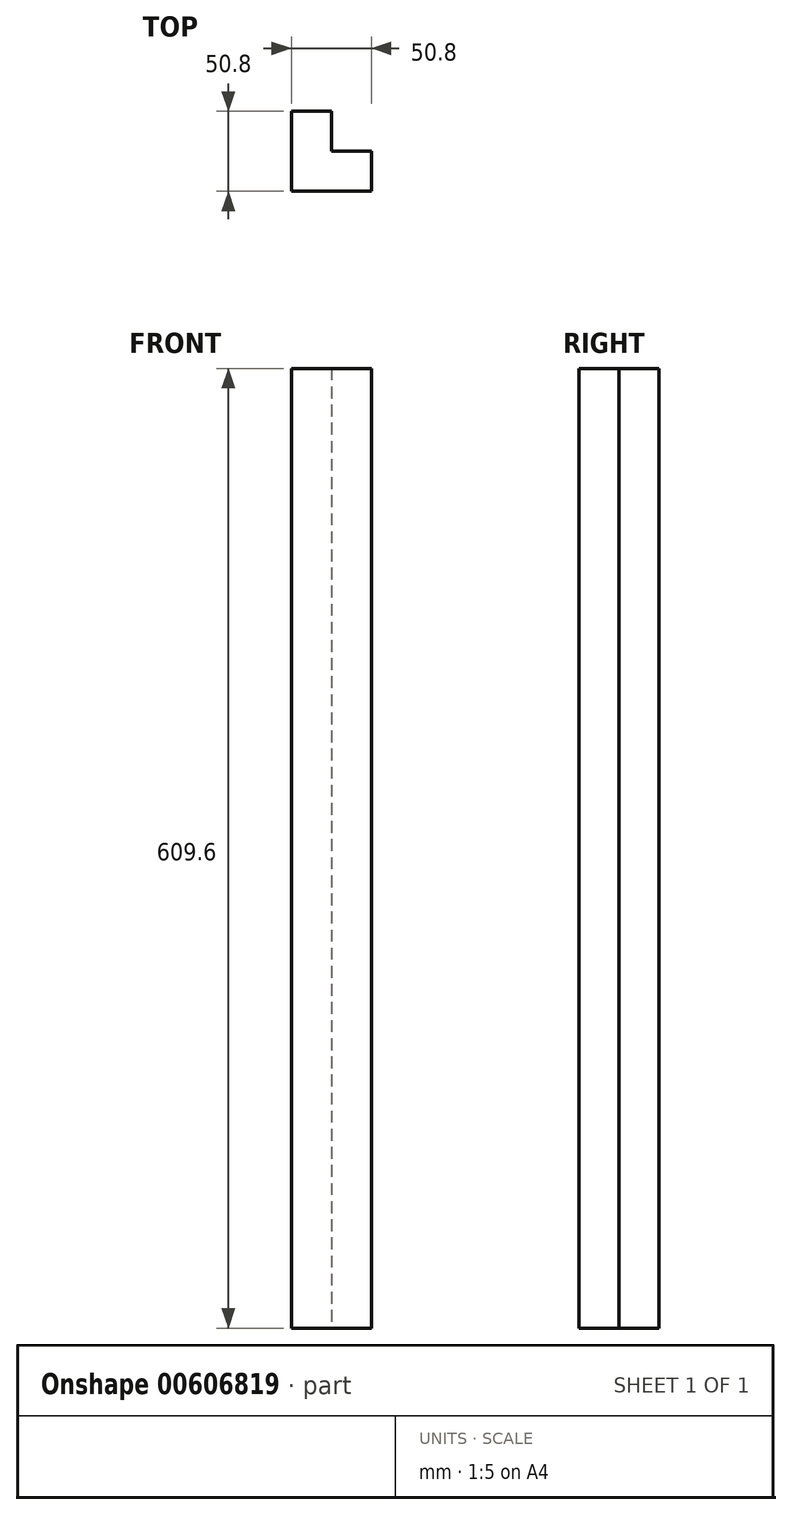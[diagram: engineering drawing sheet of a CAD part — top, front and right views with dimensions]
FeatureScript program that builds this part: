
annotation { "Feature Type Name" : "Feature", "Feature Type Description" : "" }
export const myFeature = defineFeature(function(context is Context, id is Id, definition is map)
    precondition{}
    {
        {
            var Q0;
            Q0=qCreatedBy(makeId("Top.planeOp"),FACE);
            var sketch = newSketch(context, id + "F0", { "sketchPlane" : qUnion([Q0])});
            skLineSegment(sketch, "E0", {"start": v(0, 0) * mm, "end": v(50.8, 0) * mm});
            skLineSegment(sketch, "E1", {"start": v(0, 0) * mm, "end": v(0, 50.8) * mm});
            skLineSegment(sketch, "E2", {"start": v(0, 50.8) * mm, "end": v(25.4, 50.8) * mm});
            skLineSegment(sketch, "E3", {"start": v(50.8, 0) * mm, "end": v(50.8, 25.4) * mm});
            skLineSegment(sketch, "E4", {"start": v(50.8, 25.4) * mm, "end": v(25.4, 25.4) * mm});
            skLineSegment(sketch, "E5", {"start": v(25.4, 50.8) * mm, "end": v(25.4, 25.4) * mm});
            skLineSegment(sketch, "E6", {"start": v(25.4, 25.4) * mm, "end": v(0, 0) * mm});
            skSolve(sketch);
        }
        {
            var Q0;
            Q0 = qSketchRegion(id + "F0", true);
            extrude(context, id + "F1", {"entities" : qUnion([Q0]), "depth" : 609.6 * mm, "offsetDistance" : 25.4 * mm});
        }
    });
